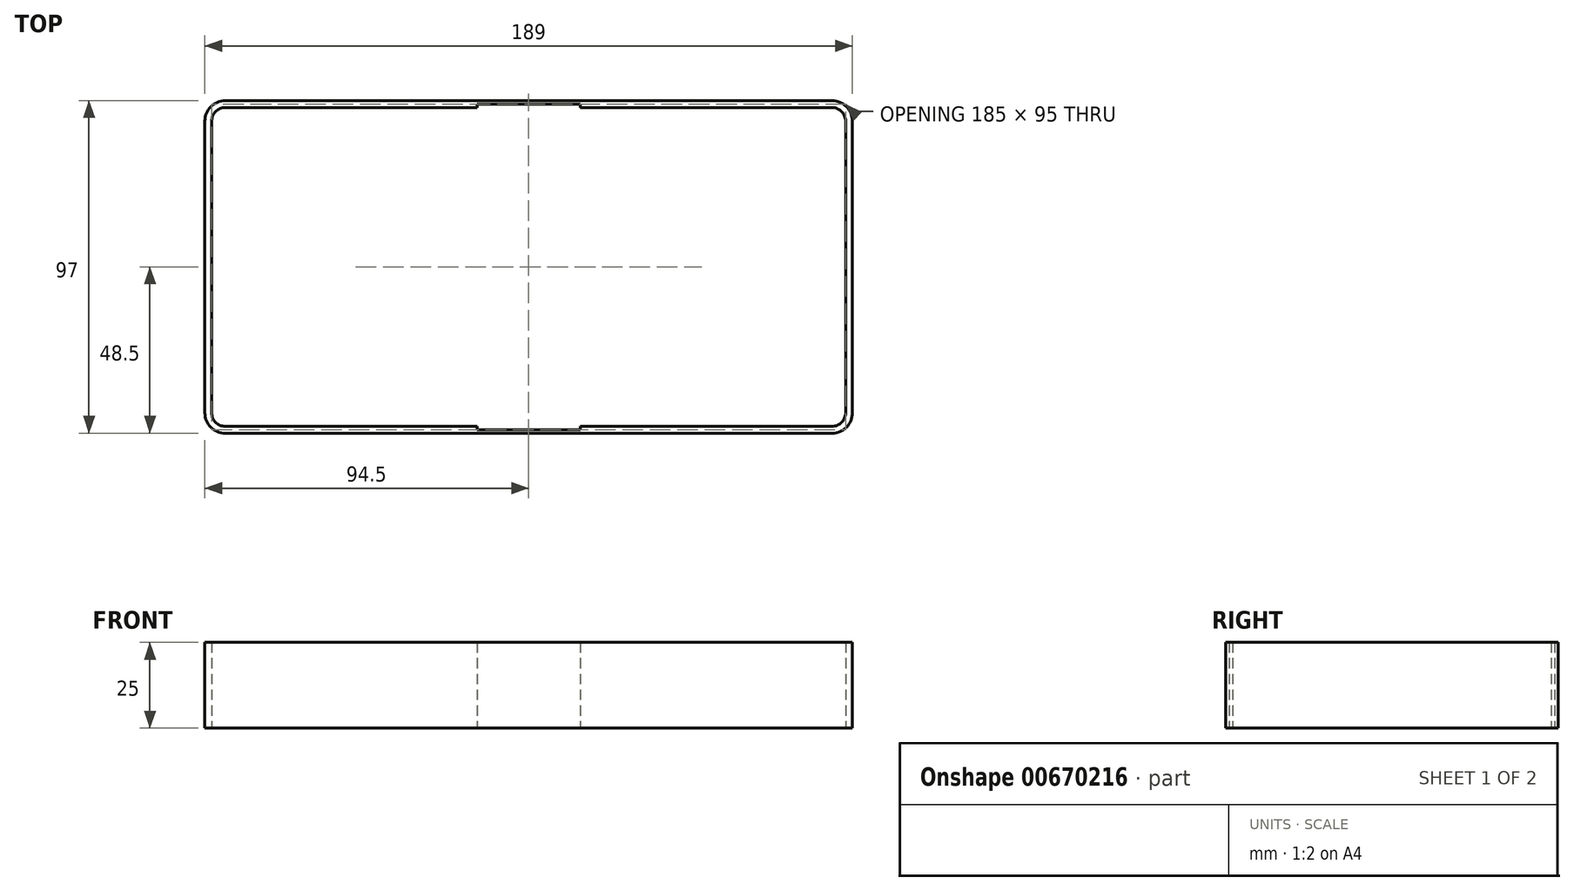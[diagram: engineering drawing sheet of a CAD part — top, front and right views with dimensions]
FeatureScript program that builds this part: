
annotation { "Feature Type Name" : "Feature", "Feature Type Description" : "" }
export const myFeature = defineFeature(function(context is Context, id is Id, definition is map)
    precondition{}
    {
        {
            var Q0;
            Q0=qCreatedBy(makeId("Top.planeOp"),FACE);
            var sketch = newSketch(context, id + "F0", { "sketchPlane" : qUnion([Q0])});
            skLineSegment(sketch, "E0.bottom", {"start": v(4, 0) * mm, "end": v(77.5, 0) * mm});
            skLineSegment(sketch, "E0.top", {"start": v(4, 93) * mm, "end": v(77.5, 93) * mm});
            skLineSegment(sketch, "E0.left", {"start": v(0, 4) * mm, "end": v(0, 89) * mm});
            skLineSegment(sketch, "E0.right", {"start": v(185, 4) * mm, "end": v(185, 89) * mm});
            skLineSegment(sketch, "E1", {"start": v(77.5, 93) * mm, "end": v(77.5, 94) * mm});
            skLineSegment(sketch, "E2", {"start": v(77.5, 94) * mm, "end": v(107.5, 94) * mm});
            skLineSegment(sketch, "E3", {"start": v(107.5, 94) * mm, "end": v(107.5, 93) * mm});
            skLineSegment(sketch, "E4", {"start": v(77.5, 0) * mm, "end": v(77.5, -1) * mm});
            skLineSegment(sketch, "E5", {"start": v(77.5, -1) * mm, "end": v(107.5, -1) * mm});
            skLineSegment(sketch, "E6", {"start": v(107.5, -1) * mm, "end": v(107.5, 0) * mm});
            skPoint(sketch, "E7.visualSharp", {"position": v(0, 93) * mm});
            skArc(sketch, "E7.filletArc", {"start": v(4, 93) * mm, "mid": v(1.17, 91.83) * mm, "end": v(0, 89) * mm});
            skPoint(sketch, "E8.visualSharp", {"position": v(185, 93) * mm});
            skArc(sketch, "E8.filletArc", {"start": v(185, 89) * mm, "mid": v(183.83, 91.83) * mm, "end": v(181, 93) * mm});
            skPoint(sketch, "E9.visualSharp", {"position": v(185, 0) * mm});
            skArc(sketch, "E9.filletArc", {"start": v(181, 0) * mm, "mid": v(183.83, 1.17) * mm, "end": v(185, 4) * mm});
            skPoint(sketch, "E10.visualSharp", {"position": v(0, 0) * mm});
            skArc(sketch, "E10.filletArc", {"start": v(0, 4) * mm, "mid": v(1.17, 1.17) * mm, "end": v(4, 0) * mm});
            skLineSegment(sketch, "E11.trimOffspring", {"start": v(107.5, 0) * mm, "end": v(181, 0) * mm});
            skPoint(sketch, "E12.end.orphan", {"position": v(92.5, 0) * mm});
            skPoint(sketch, "E12.start.orphan", {"position": v(92.5, 93) * mm});
            skLineSegment(sketch, "E13.trimOffspring", {"start": v(107.5, 93) * mm, "end": v(181, 93) * mm});
            skLineSegment(sketch, "E14.0", {"start": v(4, 95) * mm, "end": v(77.5, 95) * mm});
            skLineSegment(sketch, "E14.1", {"start": v(4, -2) * mm, "end": v(77.5, -2) * mm});
            skArc(sketch, "E14.2", {"start": v(-2, 4) * mm, "mid": v(-0.24, -0.24) * mm, "end": v(4, -2) * mm});
            skLineSegment(sketch, "E14.3", {"start": v(-2, 4) * mm, "end": v(-2, 89) * mm});
            skArc(sketch, "E14.4", {"start": v(4, 95) * mm, "mid": v(-0.24, 93.24) * mm, "end": v(-2, 89) * mm});
            skLineSegment(sketch, "E15.0", {"start": v(107.5, -2) * mm, "end": v(181, -2) * mm});
            skLineSegment(sketch, "E15.1", {"start": v(107.5, 95) * mm, "end": v(181, 95) * mm});
            skArc(sketch, "E15.2", {"start": v(187, 89) * mm, "mid": v(185.24, 93.24) * mm, "end": v(181, 95) * mm});
            skLineSegment(sketch, "E15.3", {"start": v(187, 4) * mm, "end": v(187, 89) * mm});
            skArc(sketch, "E15.4", {"start": v(181, -2) * mm, "mid": v(185.24, -0.24) * mm, "end": v(187, 4) * mm});
            skLineSegment(sketch, "E16", {"start": v(77.5, 95) * mm, "end": v(107.5, 95) * mm});
            skLineSegment(sketch, "E17", {"start": v(77.5, -2) * mm, "end": v(107.5, -2) * mm});
            skSolve(sketch);
        }
        {
            var Q0;
            Q0=makeQuery(id+"F0.imprint","IMPRINT",FACE,{"disambiguationData":[TD([[makeQuery(id+"F0.imprint","IMPRINT",EDGE,{"derivedFrom":sQuery(id+"F0.wireOp",EDGE,"E0.bottom")}),-1.0]])]});
            extrude(context, id + "F1", {"entities" : qUnion([Q0]), "depth" : 25 * mm, "offsetDistance" : 25 * mm});
        }
    });
